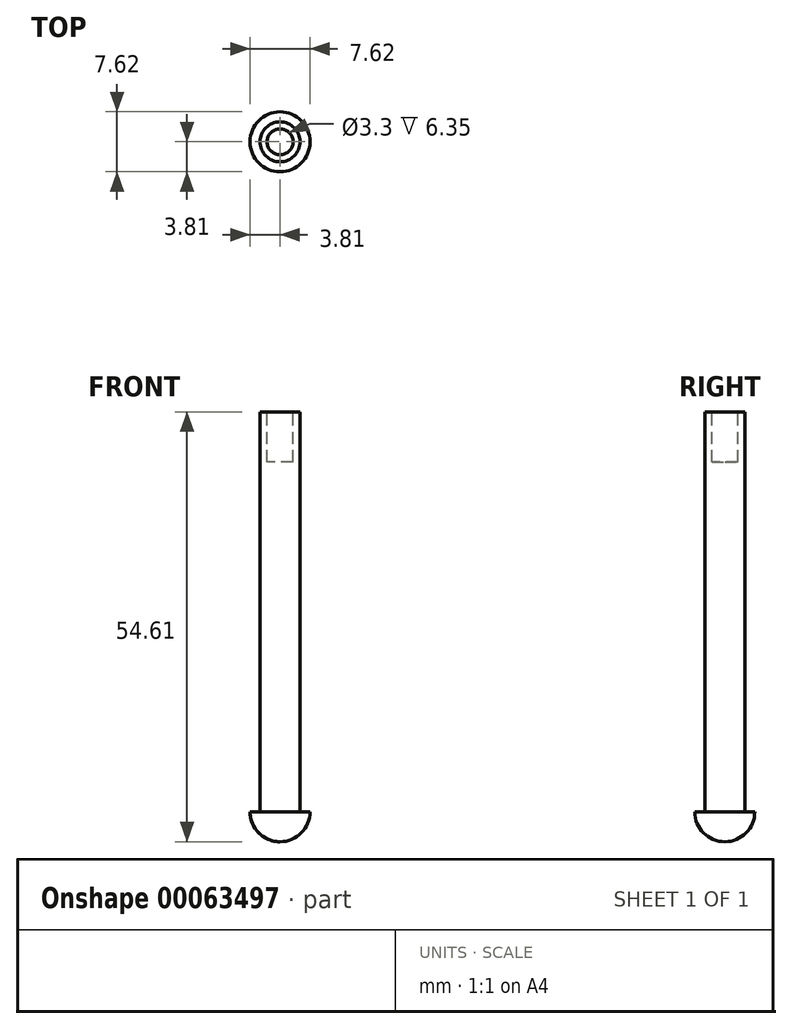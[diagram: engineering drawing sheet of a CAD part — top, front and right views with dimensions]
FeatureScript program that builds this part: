
annotation { "Feature Type Name" : "Feature", "Feature Type Description" : "" }
export const myFeature = defineFeature(function(context is Context, id is Id, definition is map)
    precondition{}
    {
        {
            var Q0;
            Q0=qCreatedBy(makeId("Top.planeOp"),FACE);
            var sketch = newSketch(context, id + "F0", { "sketchPlane" : qUnion([Q0])});
            skCircle(sketch, "E0", {"center": v(0, 0) * mm, "radius": 2.54 * mm});
            skSolve(sketch);
        }
        {
            var Q0;
            Q0 = qSketchRegion(id + "F0", true);
            extrude(context, id + "F1", {"entities" : qUnion([Q0]), "depth" : 50.8 * mm});
        }
        {
            var Q0;
            Q0=makeQuery(id+"F1.opExtrude","CAP_FACE",FACE,{"disambiguationData":[OSD([sQuery(id+"F0.wireOp",EDGE,"E0")])],"isStart":false});
            var sketch = newSketch(context, id + "F2", { "sketchPlane" : qUnion([Q0])});
            skSolve(sketch);
        }
        {
            var Q0;
            Q0=makeQuery(id+"F2.imprint","IMPRINT",FACE,{"disambiguationData":[TD([[makeQuery(id+"F2.imprint","IMPRINT",EDGE,{"derivedFrom":makeQuery(id+"F1.opExtrude","CAP_EDGE",EDGE,{"disambiguationData":[OSD([sQuery(id+"F0.wireOp",EDGE,"E0")])],"isStart":false})}),1.0]])]});
            var sketch = newSketch(context, id + "F3", { "sketchPlane" : qUnion([Q0])});
            skCircle(sketch, "E1", {"center": v(0, 0) * mm, "radius": 1.65 * mm});
            skSolve(sketch);
        }
        {
            var Q0;
            Q0 = qSketchRegion(id + "F3", true);
            extrude(context, id + "F4", {"entities" : qUnion([Q0]), "operationType" : NewBodyOperationType.REMOVE, "oppositeDirection" : true, "depth" : 6.35 * mm});
        }
        {
            var Q0;
            Q0=makeQuery(id+"F1.opExtrude","CAP_FACE",FACE,{"disambiguationData":[OSD([sQuery(id+"F0.wireOp",EDGE,"E0")])],"isStart":true});
            var sketch = newSketch(context, id + "F5", { "sketchPlane" : qUnion([Q0])});
            skCircle(sketch, "E2", {"center": v(0, 0) * mm, "radius": 3.81 * mm});
            skSolve(sketch);
        }
        {
            var Q0;
            Q0 = qSketchRegion(id + "F5", true);
            extrude(context, id + "F6", {"entities" : qUnion([Q0]), "operationType" : NewBodyOperationType.ADD, "depth" : 3.8 * mm});
        }
        {
            var Q0;
            Q0=makeQuery(id+"F6.opExtrude","CAP_EDGE",EDGE,{"disambiguationData":[OSD([sQuery(id+"F5.wireOp",EDGE,"E2")])],"isStart":false});
            fillet(context, id + "F7", {"entities" : qUnion([Q0]), "radius" : 3.8 * mm, "tangentPropagation" : true, "allowEdgeOverflow" : false});
        }
    });
